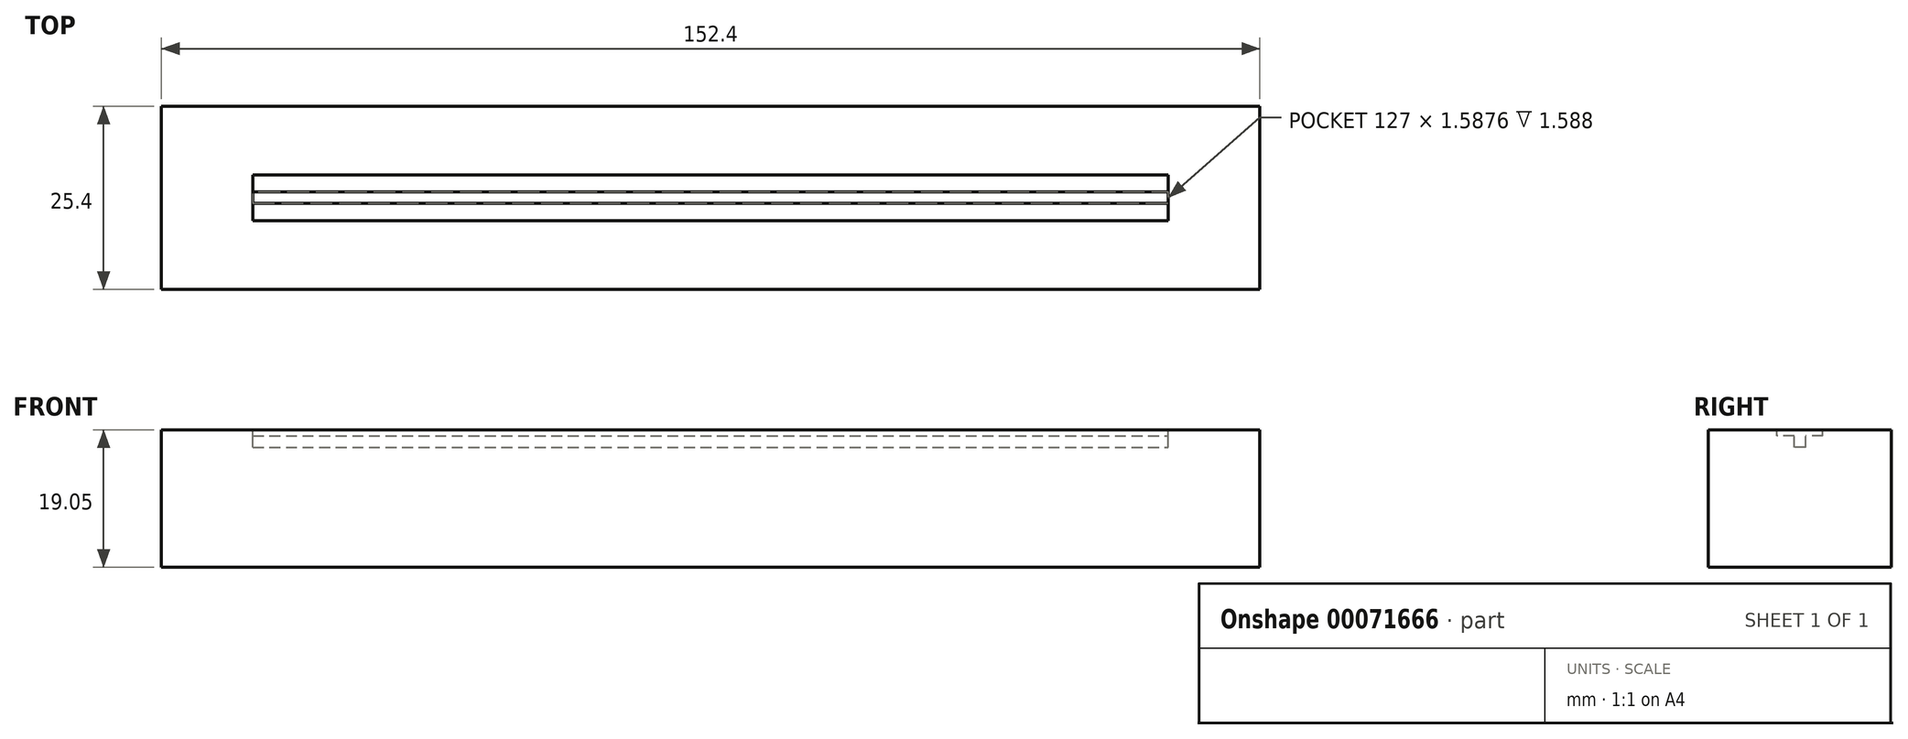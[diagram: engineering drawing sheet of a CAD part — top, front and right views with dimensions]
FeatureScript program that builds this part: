
annotation { "Feature Type Name" : "Feature", "Feature Type Description" : "" }
export const myFeature = defineFeature(function(context is Context, id is Id, definition is map)
    precondition{}
    {
        {
            var Q0;
            Q0=qCreatedBy(makeId("Top.planeOp"),FACE);
            var sketch = newSketch(context, id + "F0", { "sketchPlane" : qUnion([Q0])});
            skLineSegment(sketch, "E0.bottom", {"start": v(0, 0) * mm, "end": v(152.4, 0) * mm});
            skLineSegment(sketch, "E0.top", {"start": v(0, 25.4) * mm, "end": v(152.4, 25.4) * mm});
            skLineSegment(sketch, "E0.left", {"start": v(0, 0) * mm, "end": v(0, 25.4) * mm});
            skLineSegment(sketch, "E0.right", {"start": v(152.4, 0) * mm, "end": v(152.4, 25.4) * mm});
            skSolve(sketch);
        }
        {
            var Q0;
            Q0 = qSketchRegion(id + "F0", true);
            extrude(context, id + "F1", {"entities" : qUnion([Q0]), "depth" : 19.05 * mm});
        }
        {
            var Q0;
            Q0=makeQuery(id+"F1.opExtrude","CAP_FACE",FACE,{"disambiguationData":[OSD([sQuery(id+"F0.wireOp",EDGE,"E0.bottom"),sQuery(id+"F0.wireOp",EDGE,"E0.top"),sQuery(id+"F0.wireOp",EDGE,"E0.left"),sQuery(id+"F0.wireOp",EDGE,"E0.right")])],"isStart":false});
            var sketch = newSketch(context, id + "F2", { "sketchPlane" : qUnion([Q0])});
            skLineSegment(sketch, "E1", {"start": v(12.7, 9.53) * mm, "end": v(139.7, 9.53) * mm});
            skLineSegment(sketch, "E2", {"start": v(139.7, 9.53) * mm, "end": v(139.7, 15.88) * mm});
            skLineSegment(sketch, "E3", {"start": v(139.7, 15.88) * mm, "end": v(12.7, 15.88) * mm});
            skLineSegment(sketch, "E4", {"start": v(12.7, 15.88) * mm, "end": v(12.7, 9.53) * mm});
            skSolve(sketch);
        }
        {
            var Q0;
            Q0 = qSketchRegion(id + "F2", true);
            extrude(context, id + "F3", {"entities" : qUnion([Q0]), "operationType" : NewBodyOperationType.REMOVE, "oppositeDirection" : true, "depth" : 0.81 * mm});
        }
        {
            var Q0;
            Q0=makeQuery(id+"F3.boolean.opBoolean","COPY",FACE,{"derivedFrom":makeQuery(id+"F3.opExtrude","CAP_FACE",FACE,{"disambiguationData":[OSD([sQuery(id+"F2.wireOp",EDGE,"E1"),sQuery(id+"F2.wireOp",EDGE,"E2"),sQuery(id+"F2.wireOp",EDGE,"E3"),sQuery(id+"F2.wireOp",EDGE,"E4")])],"isStart":false})});
            var sketch = newSketch(context, id + "F4", { "sketchPlane" : qUnion([Q0])});
            skLineSegment(sketch, "E5", {"start": v(12.7, 11.9) * mm, "end": v(139.7, 11.9) * mm});
            skLineSegment(sketch, "E6", {"start": v(12.7, 13.5) * mm, "end": v(139.7, 13.5) * mm});
            skLineSegment(sketch, "E7", {"start": v(139.7, 13.5) * mm, "end": v(139.7, 11.9) * mm});
            skLineSegment(sketch, "E8", {"start": v(12.7, 13.5) * mm, "end": v(12.7, 11.9) * mm});
            skSolve(sketch);
        }
        {
            var Q0;
            Q0 = qSketchRegion(id + "F4", true);
            extrude(context, id + "F5", {"entities" : qUnion([Q0]), "operationType" : NewBodyOperationType.REMOVE, "oppositeDirection" : true, "depth" : 1.59 * mm});
        }
    });
